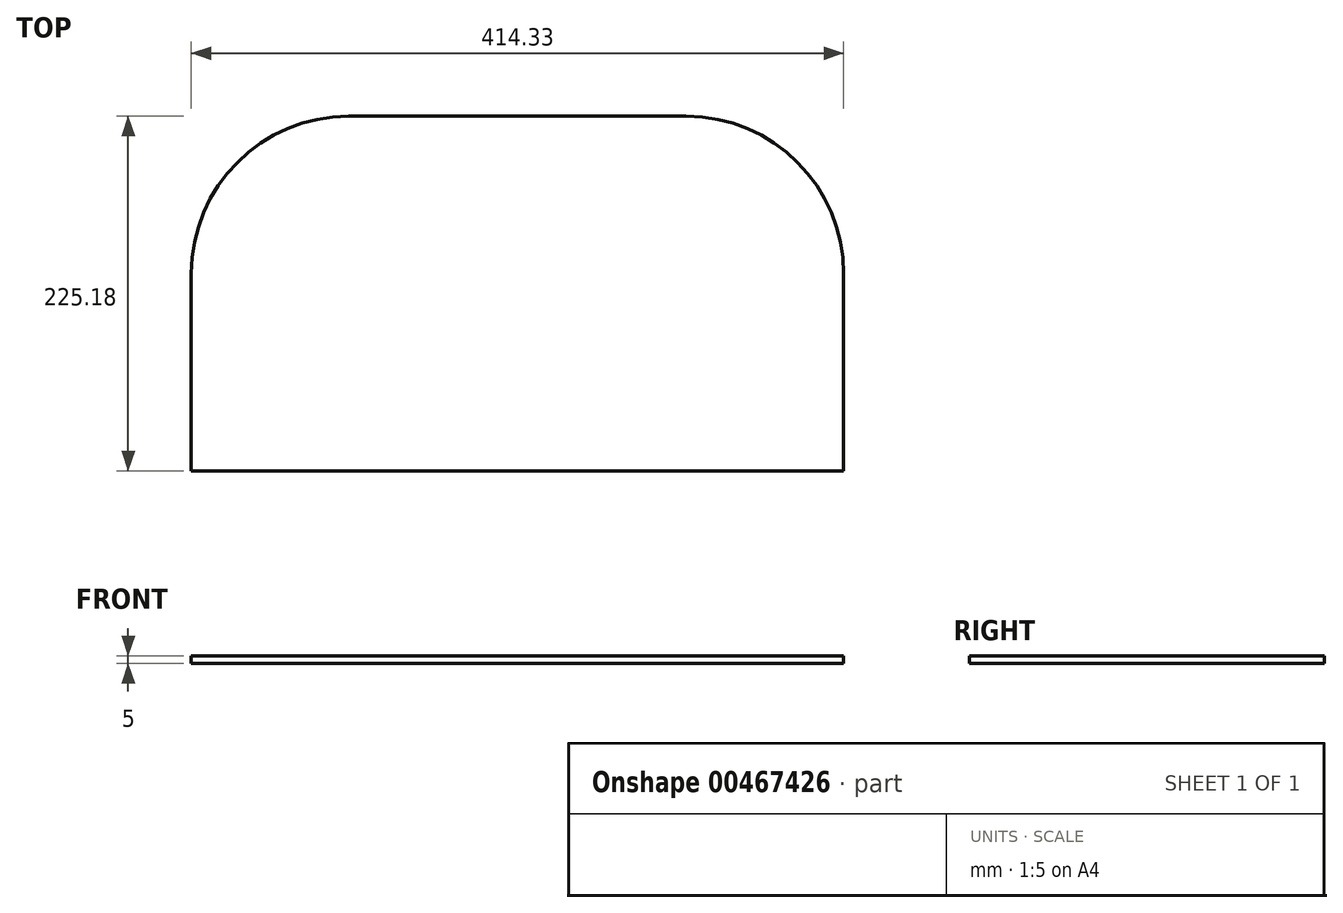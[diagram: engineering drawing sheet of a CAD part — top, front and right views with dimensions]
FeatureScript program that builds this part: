
annotation { "Feature Type Name" : "Feature", "Feature Type Description" : "" }
export const myFeature = defineFeature(function(context is Context, id is Id, definition is map)
    precondition{}
    {
        {
            var Q0;
            Q0=qCreatedBy(makeId("Top.planeOp"),FACE);
            var sketch = newSketch(context, id + "F0", { "sketchPlane" : qUnion([Q0])});
            skLineSegment(sketch, "E0.bottom", {"start": v(-117.49, 164.24) * mm, "end": v(96.84, 164.24) * mm});
            skLineSegment(sketch, "E0.top", {"start": v(-217.49, -60.94) * mm, "end": v(196.84, -60.94) * mm});
            skLineSegment(sketch, "E0.left", {"start": v(-217.49, 64.24) * mm, "end": v(-217.49, -60.94) * mm});
            skLineSegment(sketch, "E0.right", {"start": v(196.84, 64.24) * mm, "end": v(196.84, -60.94) * mm});
            skPoint(sketch, "E1.visualSharp", {"position": v(-217.49, 164.24) * mm});
            skArc(sketch, "E1.filletArc", {"start": v(-117.49, 164.24) * mm, "mid": v(-188.2, 134.96) * mm, "end": v(-217.49, 64.24) * mm});
            skPoint(sketch, "E2.visualSharp", {"position": v(196.84, 164.24) * mm});
            skArc(sketch, "E2.filletArc", {"start": v(196.84, 64.24) * mm, "mid": v(167.55, 134.96) * mm, "end": v(96.84, 164.24) * mm});
            skSolve(sketch);
        }
        {
            var Q0;
            Q0=makeQuery(id+"F0.imprint","IMPRINT",FACE,{"disambiguationData":[TD([[makeQuery(id+"F0.imprint","IMPRINT",EDGE,{"derivedFrom":sQuery(id+"F0.wireOp",EDGE,"E0.bottom")}),-1.0]])]});
            extrude(context, id + "F1", {"entities" : qUnion([Q0]), "depth" : 5 * mm});
        }
    });
